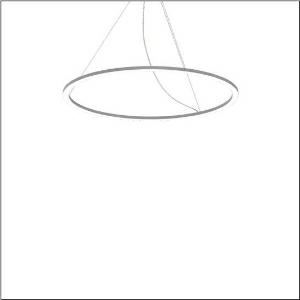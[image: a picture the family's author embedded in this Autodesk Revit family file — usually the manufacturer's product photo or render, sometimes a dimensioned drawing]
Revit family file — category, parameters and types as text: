
# Revit family: silica_r__21_ring-d_5pjbd3d1204a_4b66
name_source: partatom
category: Lighting Fixtures
units: mm (PartAtom-declared; Revit-internal decimal feet)

## family parameters
Cut with Voids When Loaded = No
Host = Face
Light Source = No
Part Type = Normal
Room Calculation Point = No
Round Connector Dimension = Use Diameter
Shared = No

## types (1)
- Silica® 21 Ring-D (1 x LED, 8050 lm, 94 W, 3000K)
    Apparent Load = 94 VA
    CIE Flux Codes = 37 69 92 100 100
    Color Rendering = 80
    Color Temperature = 3000K
    Default Elevation = 1800 mm
    Description = Silica® 21 Ring-D, suspended luminaire, of PMMA, frosted, light emission: ring underside luminous distribution, primary light characteristic: symmetric, installation type: suspended mounting, LED, rated luminous flux: 8.050lm, luminous efficacy: 86lm/W, light colour: 830, colour temperature: 3000K, control gear: DALI 2, with terminal, 5-pole, mains connection: 230V, AC/DC, 0/50..60Hz, rated input power: 94W, housing, of extruded aluminium section, metallic grey (RAL 9006), diameter: 1.100mm, ceiling canopy, metallic grey (RAL 9006), protection rating (lamp compartment): IP40, insulation class (complete): insulation class I (protective earthing), certification: CE, impact resistance: IK02, permissible operating ambient temperature: 0..+35°C, packaging unit: 1 piece
    Height = 25 mm  [stored 0.082021 ft]
    Lamp = 1 x LED
    Lamp Light Flux = 8050 lm
    Lamp Power = 94 W
    Lamp count = 1
    Length = 1100 mm
    Luminous efficacy = 86 lm/W
    Manufacturer = Siteco
    ModVariant = No
    Model = 5PJBD3D1204A
    Mounting Place = Ceiling
    Mounting Type = Pendant
    Number of Poles = 1
    OnlyDefault = Yes
    Power Factor = 1
    Product Name = Silica® 21 Ring-D
    Product group = suspended luminaire
    ProductGroupID = 905
    Protection Class = Protection class I
    Protection Degree = IP 40
    RLX_Detail_Level = 1
    RLX_Emergency_Light_Flux = 0 lm
    RLX_Emergency_Type = 0
    RLX_Emergency_Type_DB = No
    RlxData = <blob elided: 14593 chars, md5=ebf16394>
    Socket = socket
    Standby Power = 0 W
    System Light Flux = 8050 lm
    System Power = 94 W
    Type Comments = Product without accessories
    Type Image = l_1251746.jpg
    URL = http://relux.com
    VarID = ---
    Voltage = 0 V
    Weight = 0.00 kg
    Width = 0 mm  [stored 0 ft]

note: [stored X ft] marks values corroborated as IEEE doubles in the binary element streams (Revit-internal decimal feet)

## geometry (parser evidence)
native form markers: Blend x4, Sweep x11
no freeform markers — native parametric forms only
